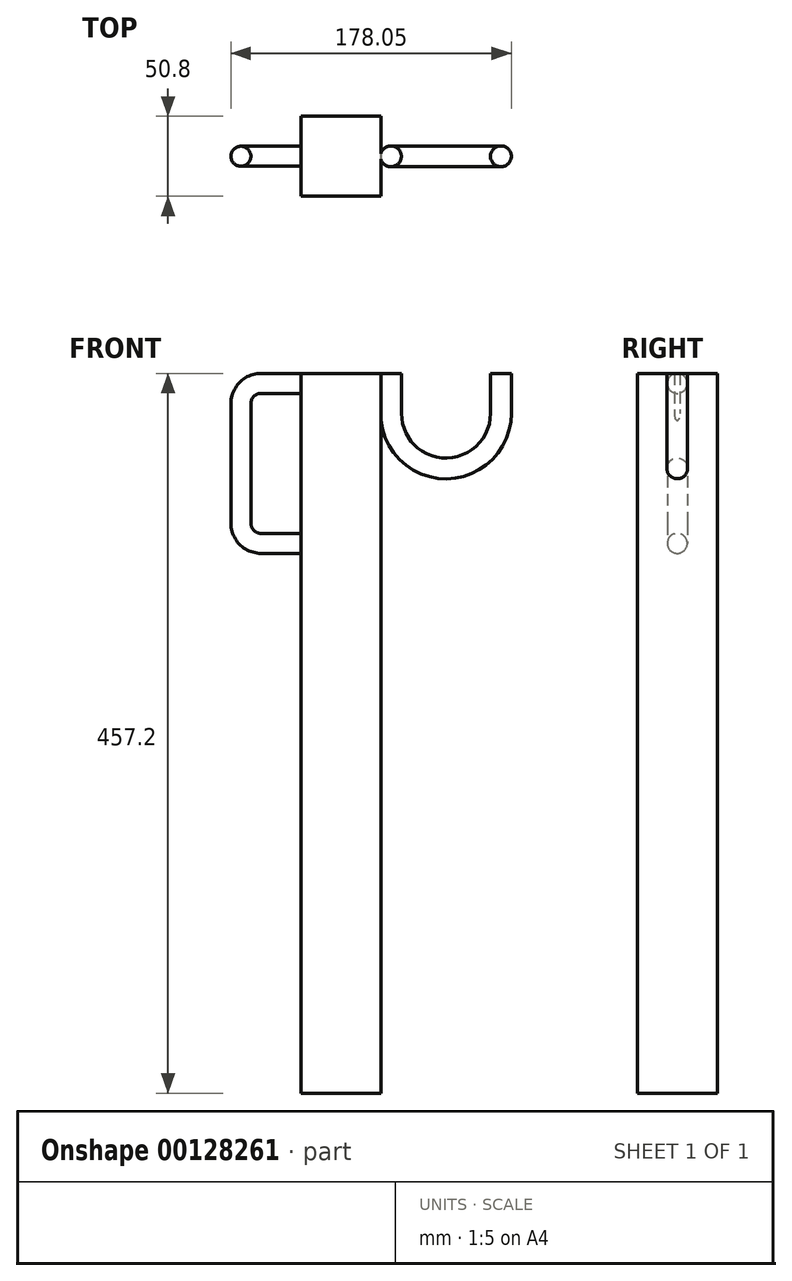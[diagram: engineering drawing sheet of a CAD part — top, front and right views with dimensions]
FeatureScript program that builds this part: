
annotation { "Feature Type Name" : "Feature", "Feature Type Description" : "" }
export const myFeature = defineFeature(function(context is Context, id is Id, definition is map)
    precondition{}
    {
        {
            var Q0;
            Q0=qCreatedBy(makeId("Top.planeOp"),FACE);
            var sketch = newSketch(context, id + "F0", { "sketchPlane" : qUnion([Q0])});
            skLineSegment(sketch, "E0.bottom", {"start": v(25.4, 25.4) * mm, "end": v(-25.4, 25.4) * mm});
            skLineSegment(sketch, "E0.top", {"start": v(25.4, -25.4) * mm, "end": v(-25.4, -25.4) * mm});
            skLineSegment(sketch, "E0.left", {"start": v(25.4, 25.4) * mm, "end": v(25.4, -25.4) * mm});
            skLineSegment(sketch, "E0.right", {"start": v(-25.4, 25.4) * mm, "end": v(-25.4, -25.4) * mm});
            skPoint(sketch, "E0.middle", {"position": v(0, 0) * mm});
            skSolve(sketch);
        }
        {
            var Q0;
            Q0=makeQuery(id+"F0.imprint","IMPRINT",FACE,{"disambiguationData":[TD([[makeQuery(id+"F0.imprint","IMPRINT",EDGE,{"derivedFrom":sQuery(id+"F0.wireOp",EDGE,"E0.bottom")}),1.0]])]});
            extrude(context, id + "F1", {"entities" : qUnion([Q0]), "depth" : 203.2 * mm, "hasSecondDirection" : true, "secondDirectionOppositeDirection" : true, "secondDirectionDepth" : 254 * mm});
        }
        {
            var Q0;
            Q0=qCreatedBy(makeId("Front.planeOp"),FACE);
            var sketch = newSketch(context, id + "F2", { "sketchPlane" : qUnion([Q0])});
            skLineSegment(sketch, "E1", {"start": v(25.4, 203.2) * mm, "end": v(101.6, 203.2) * mm, "construction": true});
            skLineSegment(sketch, "E2", {"start": v(101.6, 203.2) * mm, "end": v(101.6, 177.8) * mm});
            skLineSegment(sketch, "E3", {"start": v(31.75, 203.2) * mm, "end": v(31.75, 177.8) * mm});
            skArc(sketch, "E4", {"start": v(31.75, 177.8) * mm, "mid": v(66.67, 142.88) * mm, "end": v(101.6, 177.8) * mm});
            skSolve(sketch);
        }
        {
            var Q0;
            Q0=makeQuery(id+"F1.opExtrude","CAP_FACE",FACE,{"disambiguationData":[OSD([sQuery(id+"F0.wireOp",EDGE,"E0.bottom"),sQuery(id+"F0.wireOp",EDGE,"E0.top"),sQuery(id+"F0.wireOp",EDGE,"E0.left"),sQuery(id+"F0.wireOp",EDGE,"E0.right")])],"isStart":false});
            var sketch = newSketch(context, id + "F3", { "sketchPlane" : qUnion([Q0])});
            skPoint(sketch, "E5.0", {"position": v(31.75, 0) * mm});
            skLineSegment(sketch, "E6.0", {"start": v(25.4, 25.4) * mm, "end": v(25.4, -25.4) * mm, "construction": true});
            skCircle(sketch, "E7", {"center": v(31.75, 0) * mm, "radius": 6.6 * mm});
            skLineSegment(sketch, "E8", {"start": v(25.4, 0) * mm, "end": v(25.15, 0) * mm, "construction": true});
            skSolve(sketch);
        }
        {
            var Q0;
            Q0 = qSketchRegion(id + "F3", true);
            var Q1;
            Q1 = qConstructionFilter(qBodyType(qCreatedBy(id + "F2" ,EDGE), BodyType.WIRE), ConstructionObject.NO);
            sweep(context, id + "F4", {"operationType" : NewBodyOperationType.ADD, "profiles" : qUnion([Q0]), "path" : qUnion([Q1])});
        }
        {
            var Q0;
            Q0=qCreatedBy(makeId("Front.planeOp"),FACE);
            var sketch = newSketch(context, id + "F5", { "sketchPlane" : qUnion([Q0])});
            skLineSegment(sketch, "E9.0", {"start": v(25.4, 203.2) * mm, "end": v(-25.4, 203.2) * mm, "construction": true});
            skLineSegment(sketch, "E10", {"start": v(-25.4, 203.2) * mm, "end": v(-25.4, 196.85) * mm, "construction": true});
            skLineSegment(sketch, "E11", {"start": v(-25.4, 196.85) * mm, "end": v(-50.8, 196.85) * mm});
            skLineSegment(sketch, "E12", {"start": v(-63.5, 184.15) * mm, "end": v(-63.5, 107.95) * mm});
            skLineSegment(sketch, "E13", {"start": v(-50.8, 95.25) * mm, "end": v(-25.33, 95.25) * mm});
            skLineSegment(sketch, "E14", {"start": v(-25.4, 196.85) * mm, "end": v(-25.33, 95.25) * mm, "construction": true});
            skPoint(sketch, "E15.visualSharp", {"position": v(-63.5, 196.85) * mm});
            skArc(sketch, "E15.filletArc", {"start": v(-50.8, 196.85) * mm, "mid": v(-59.78, 193.13) * mm, "end": v(-63.5, 184.15) * mm});
            skPoint(sketch, "E16.visualSharp", {"position": v(-63.5, 95.25) * mm});
            skArc(sketch, "E16.filletArc", {"start": v(-63.5, 107.95) * mm, "mid": v(-59.78, 98.97) * mm, "end": v(-50.8, 95.25) * mm});
            skSolve(sketch);
        }
        {
            var Q0;
            Q0=makeQuery(id+"F1.opExtrude","SWEPT_FACE",FACE,{"disambiguationData":[OSD([sQuery(id+"F0.wireOp",EDGE,"E0.right")])]});
            var sketch = newSketch(context, id + "F6", { "sketchPlane" : qUnion([Q0])});
            skLineSegment(sketch, "E17.0", {"start": v(0, 203.2) * mm, "end": v(0, 196.85) * mm, "construction": true});
            skCircle(sketch, "E18", {"center": v(0, 196.85) * mm, "radius": 6.35 * mm});
            skSolve(sketch);
        }
        {
            var Q0;
            Q0 = qSketchRegion(id + "F6", true);
            var Q1;
            Q1 = qConstructionFilter(qBodyType(qCreatedBy(id + "F5" ,EDGE), BodyType.WIRE), ConstructionObject.NO);
            sweep(context, id + "F7", {"operationType" : NewBodyOperationType.ADD, "profiles" : qUnion([Q0]), "path" : qUnion([Q1])});
        }
    });
